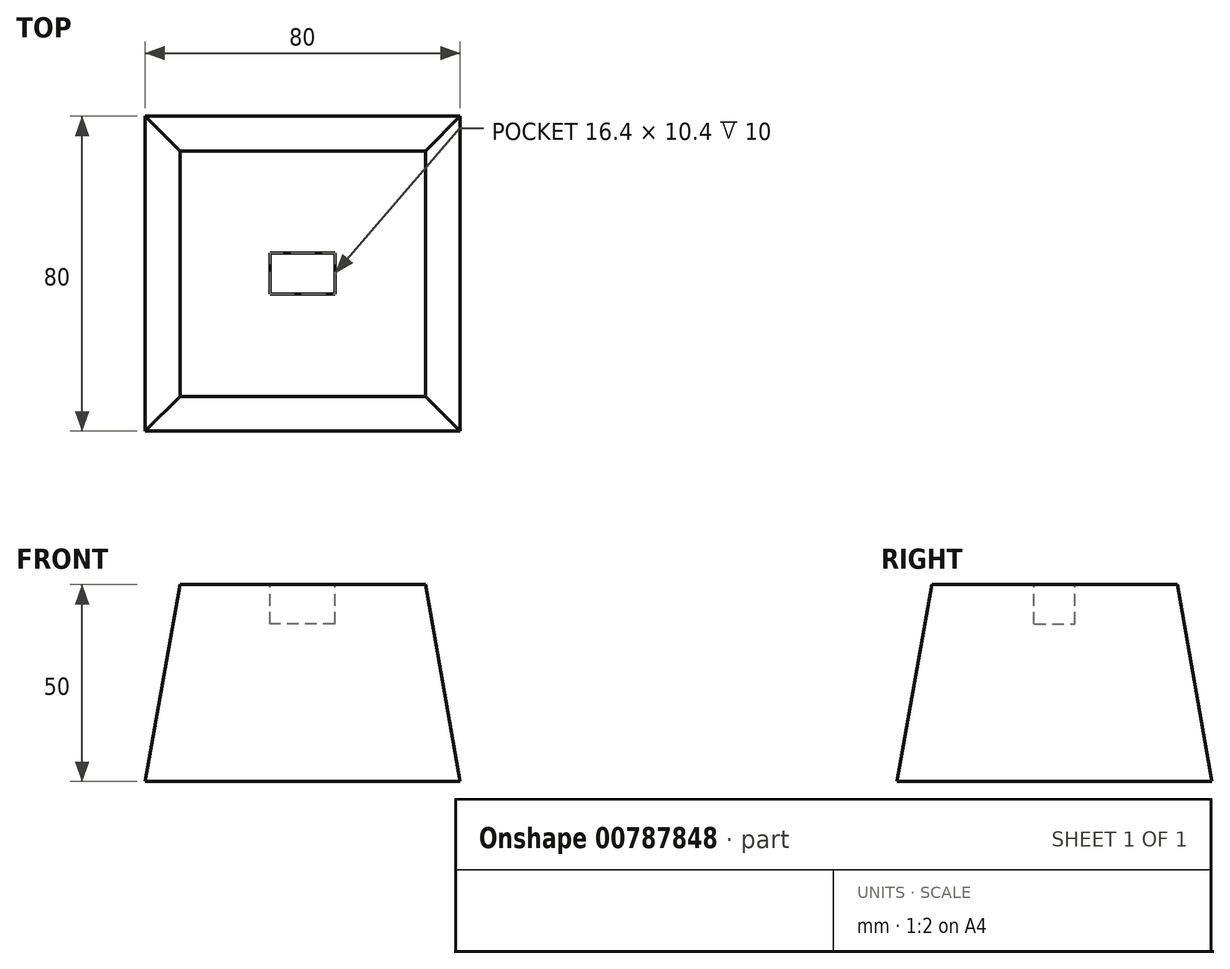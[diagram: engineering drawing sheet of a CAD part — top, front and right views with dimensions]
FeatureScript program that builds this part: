
annotation { "Feature Type Name" : "Feature", "Feature Type Description" : "" }
export const myFeature = defineFeature(function(context is Context, id is Id, definition is map)
    precondition{}
    {
        {
            var Q0;
            Q0=qCreatedBy(makeId("Top.planeOp"),FACE);
            var sketch = newSketch(context, id + "F0", { "sketchPlane" : qUnion([Q0])});
            skLineSegment(sketch, "E0.bottom", {"start": v(40, -40) * mm, "end": v(-40, -40) * mm});
            skLineSegment(sketch, "E0.top", {"start": v(40, 40) * mm, "end": v(-40, 40) * mm});
            skLineSegment(sketch, "E0.left", {"start": v(40, -40) * mm, "end": v(40, 40) * mm});
            skLineSegment(sketch, "E0.right", {"start": v(-40, -40) * mm, "end": v(-40, 40) * mm});
            skPoint(sketch, "E0.middle", {"position": v(0, 0) * mm});
            skSolve(sketch);
        }
        {
            var Q0;
            Q0 = qSketchRegion(id + "F0", true);
            extrude(context, id + "F1", {"entities" : qUnion([Q0]), "depth" : 50 * mm, "offsetDistance" : 25 * mm, "hasDraft" : true, "draftAngle" : 10 * degree, "draftPullDirection" : true});
        }
        {
            var Q0;
            Q0=makeQuery(id+"F1.opExtrude","CAP_FACE",FACE,{"disambiguationData":[OSD([sQuery(id+"F0.wireOp",EDGE,"E0.bottom"),sQuery(id+"F0.wireOp",EDGE,"E0.top"),sQuery(id+"F0.wireOp",EDGE,"E0.left"),sQuery(id+"F0.wireOp",EDGE,"E0.right")])],"isStart":false});
            var sketch = newSketch(context, id + "F2", { "sketchPlane" : qUnion([Q0])});
            skLineSegment(sketch, "E1.bottom", {"start": v(8.2, -5.2) * mm, "end": v(-8.2, -5.2) * mm});
            skLineSegment(sketch, "E1.top", {"start": v(8.2, 5.2) * mm, "end": v(-8.2, 5.2) * mm});
            skLineSegment(sketch, "E1.left", {"start": v(8.2, -5.2) * mm, "end": v(8.2, 5.2) * mm});
            skLineSegment(sketch, "E1.right", {"start": v(-8.2, -5.2) * mm, "end": v(-8.2, 5.2) * mm});
            skPoint(sketch, "E1.middle", {"position": v(0, 0) * mm});
            skSolve(sketch);
        }
        {
            var Q0;
            Q0=makeQuery(id+"F2.imprint","IMPRINT",FACE,{"disambiguationData":[TD([[makeQuery(id+"F2.imprint","IMPRINT",EDGE,{"derivedFrom":sQuery(id+"F2.wireOp",EDGE,"E1.bottom")}),-1.0]])]});
            extrude(context, id + "F3", {"entities" : qUnion([Q0]), "operationType" : NewBodyOperationType.REMOVE, "oppositeDirection" : true, "depth" : 10 * mm, "offsetDistance" : 25 * mm});
        }
    });
